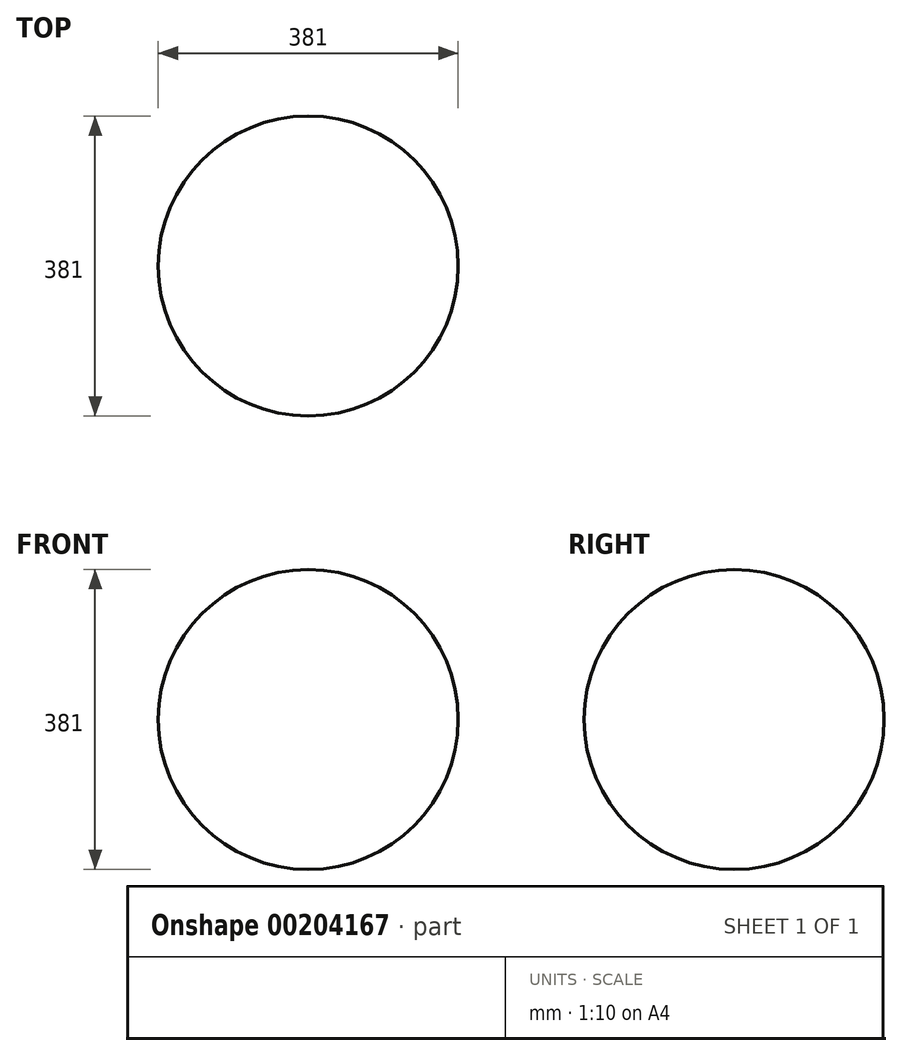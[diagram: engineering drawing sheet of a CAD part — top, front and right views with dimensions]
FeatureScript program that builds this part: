
annotation { "Feature Type Name" : "Feature", "Feature Type Description" : "" }
export const myFeature = defineFeature(function(context is Context, id is Id, definition is map)
    precondition{}
    {
        {
            var Q0;
            Q0=qCreatedBy(makeId("Top.planeOp"),FACE);
            var sketch = newSketch(context, id + "F0", { "sketchPlane" : qUnion([Q0])});
            skArc(sketch, "E0", {"start": v(0, -190.5) * mm, "mid": v(190.5, 0) * mm, "end": v(0, 190.5) * mm});
            skLineSegment(sketch, "E1", {"start": v(0, 190.5) * mm, "end": v(0, -190.5) * mm});
            skSolve(sketch);
        }
        {
            var Q0;
            Q0=makeQuery(id+"F0.imprint","IMPRINT",FACE,{"disambiguationData":[TD([[makeQuery(id+"F0.imprint","IMPRINT",EDGE,{"derivedFrom":sQuery(id+"F0.wireOp",EDGE,"E0")}),1.0]])]});
            var Q1;
            Q1=sQuery(id+"F0.wireOp",EDGE,"E1");
            revolve(context, id + "F1", {"surfaceOperationType" : NewSurfaceOperationType.NEW, "entities" : qUnion([Q0]), "axis" : qUnion([Q1]), "revolveType" : RevolveType.FULL});
        }
    });
